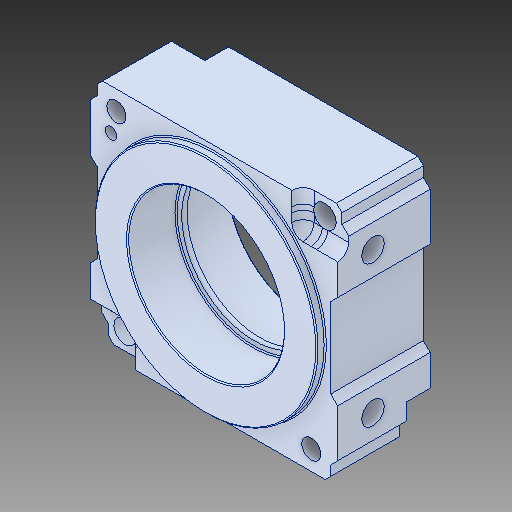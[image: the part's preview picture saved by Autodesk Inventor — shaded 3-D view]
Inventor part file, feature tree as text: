
AUTODESK INVENTOR PART (.ipt)
format: ipt  version: 2017 SP1 (Build 210196100, 196)  size: 258,560 bytes
history: native  units: in
note: dims shown in document units (in); Inventor stores cm internally (conversion verified against a paired STEP export)
features: chamfer x1
ambient origin geometry x8: Origin, YZ Plane, XZ Plane, XY Plane, X Axis, Y Axis, Z Axis, Center Point
bodies: Solid1 (feature_tree)
feature tree (1):
  chamfer  "Chamfer2"  [1 undecoded]
note: 1 required parameter value undecoded (feature->parameter linkage not recoverable at this tier; creation-order binding heuristic only, values carry confidence <= 0.55)
